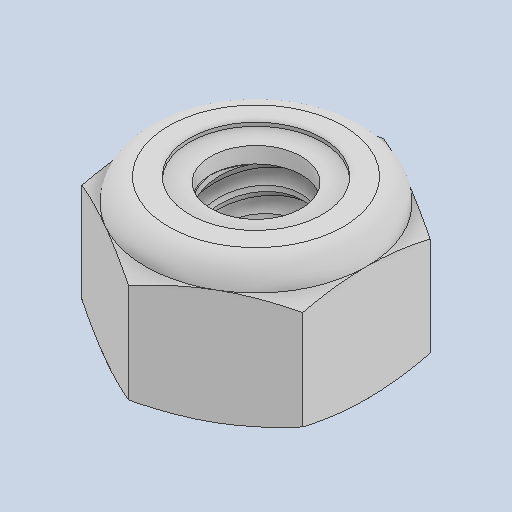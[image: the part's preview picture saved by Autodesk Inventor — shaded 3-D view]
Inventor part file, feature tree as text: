
AUTODESK INVENTOR PART (.ipt)
format: ipt  version: 2025.1 (Build 291241020, 241B)  size: 268,800 bytes
history: native  units: in
note: dims shown in document units (in); Inventor stores cm internally (conversion verified against a paired STEP export)
features: other x1, revolve x1
ambient origin geometry x8: Origin, YZ Plane, XZ Plane, XY Plane, X Axis, Y Axis, Z Axis, Center Point
bodies: Solid1 (feature_tree), Solid2 (feature_tree)
feature tree (2):
  other  "Cut-Revolve4"
  revolve  "Revolve2"  [1 undecoded]
note: 1 required parameter value undecoded (feature->parameter linkage not recoverable at this tier; creation-order binding heuristic only, values carry confidence <= 0.55)
